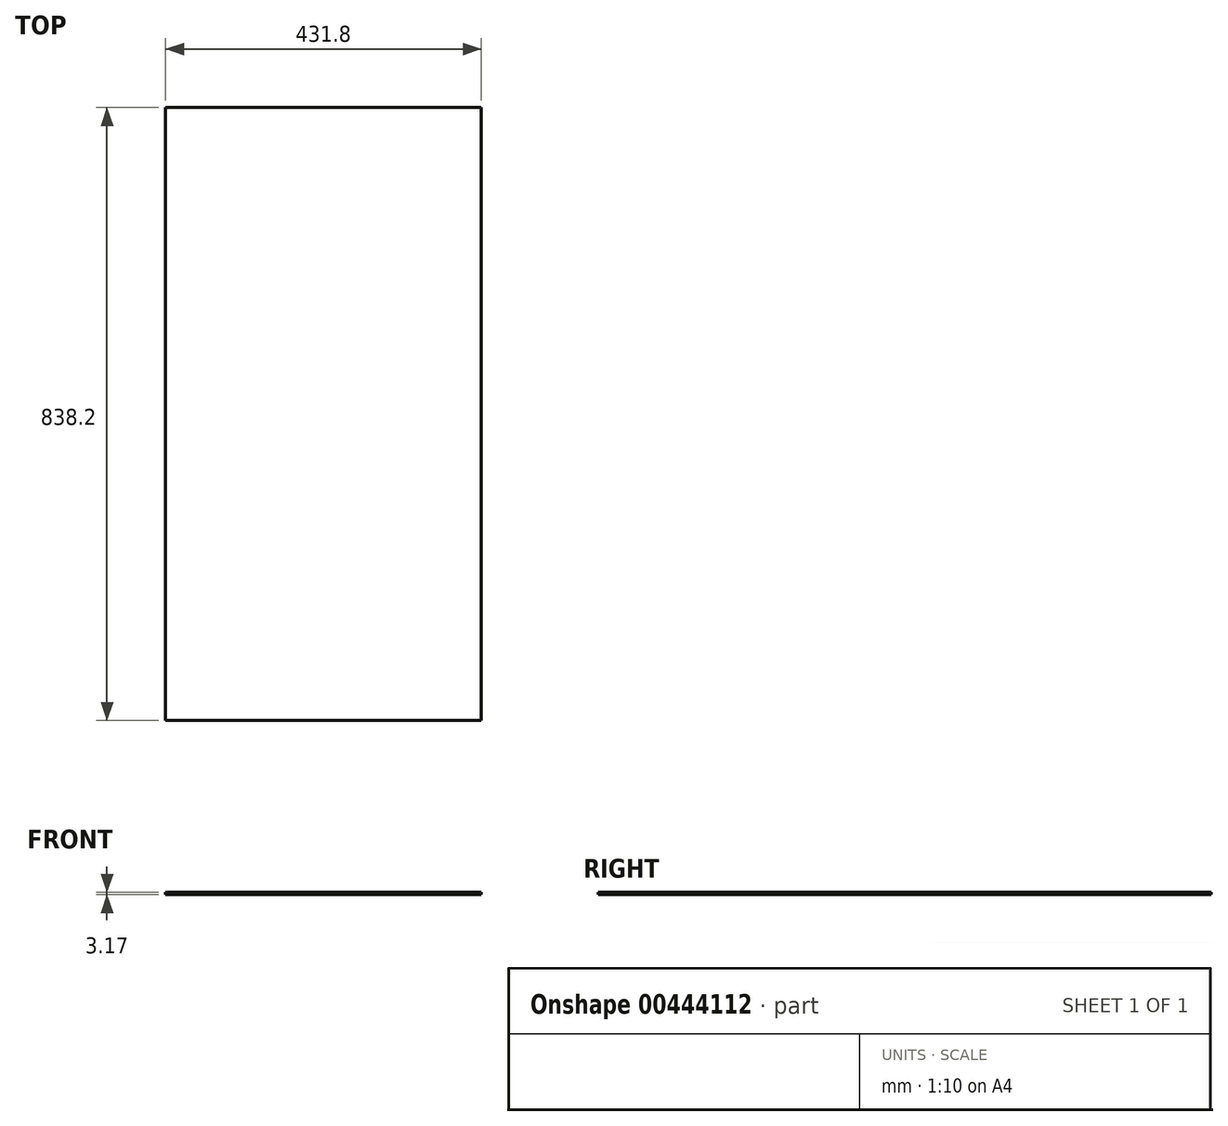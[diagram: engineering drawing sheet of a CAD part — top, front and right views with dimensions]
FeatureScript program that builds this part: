
annotation { "Feature Type Name" : "Feature", "Feature Type Description" : "" }
export const myFeature = defineFeature(function(context is Context, id is Id, definition is map)
    precondition{}
    {
        {
            var Q0;
            Q0=qCreatedBy(makeId("Top.planeOp"),FACE);
            var sketch = newSketch(context, id + "F0", { "sketchPlane" : qUnion([Q0])});
            skLineSegment(sketch, "E0.bottom", {"start": v(215.9, 419.1) * mm, "end": v(-215.9, 419.1) * mm});
            skLineSegment(sketch, "E0.top", {"start": v(215.9, -419.1) * mm, "end": v(-215.9, -419.1) * mm});
            skLineSegment(sketch, "E0.left", {"start": v(215.9, 419.1) * mm, "end": v(215.9, -419.1) * mm});
            skLineSegment(sketch, "E0.right", {"start": v(-215.9, 419.1) * mm, "end": v(-215.9, -419.1) * mm});
            skPoint(sketch, "E0.middle", {"position": v(0, 0) * mm});
            skSolve(sketch);
        }
        {
            var Q0;
            Q0=makeQuery(id+"F0.imprint","IMPRINT",FACE,{"disambiguationData":[TD([[makeQuery(id+"F0.imprint","IMPRINT",EDGE,{"derivedFrom":sQuery(id+"F0.wireOp",EDGE,"E0.bottom")}),1.0]])]});
            extrude(context, id + "F1", {"entities" : qUnion([Q0]), "depth" : 3.17 * mm});
        }
    });
